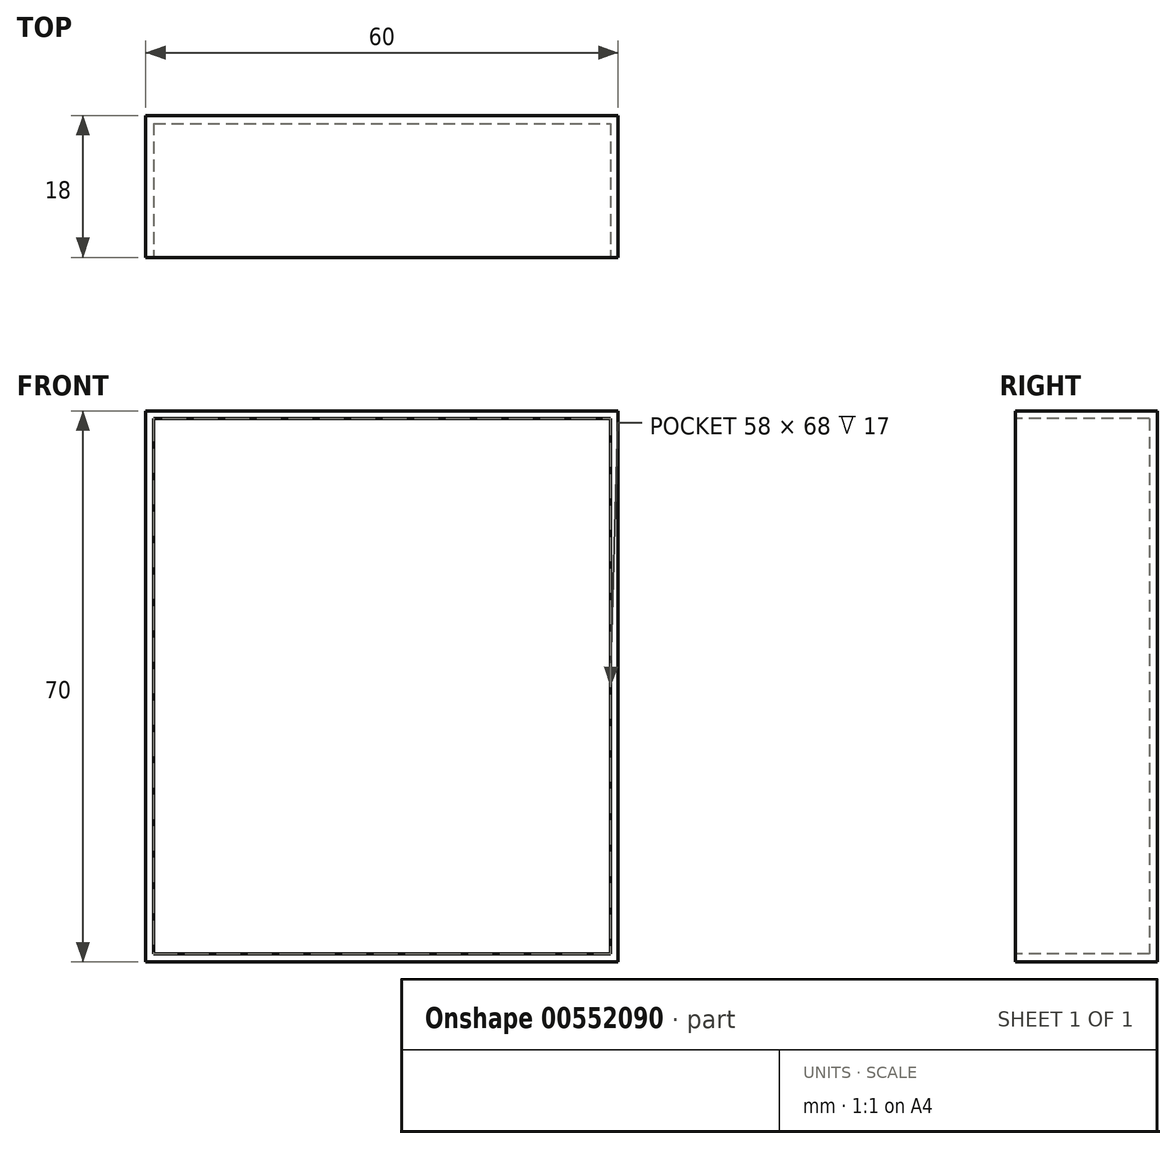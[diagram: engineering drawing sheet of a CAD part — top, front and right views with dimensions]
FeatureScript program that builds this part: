
annotation { "Feature Type Name" : "Feature", "Feature Type Description" : "" }
export const myFeature = defineFeature(function(context is Context, id is Id, definition is map)
    precondition{}
    {
        {
            var Q0;
            Q0=qCreatedBy(makeId("Front.planeOp"),FACE);
            var sketch = newSketch(context, id + "F0", { "sketchPlane" : qUnion([Q0])});
            skLineSegment(sketch, "E0.bottom", {"start": v(-30, 35) * mm, "end": v(30, 35) * mm});
            skLineSegment(sketch, "E0.top", {"start": v(-30, -35) * mm, "end": v(30, -35) * mm});
            skLineSegment(sketch, "E0.left", {"start": v(-30, 35) * mm, "end": v(-30, -35) * mm});
            skLineSegment(sketch, "E0.right", {"start": v(30, 35) * mm, "end": v(30, -35) * mm});
            skPoint(sketch, "E0.middle", {"position": v(0, 0) * mm});
            skSolve(sketch);
        }
        {
            var Q0;
            Q0 = qSketchRegion(id + "F0", true);
            extrude(context, id + "F1", {"entities" : qUnion([Q0]), "oppositeDirection" : true, "depth" : 18 * mm, "offsetDistance" : 25.4 * mm});
        }
        {
            var Q0;
            Q0=makeQuery(id+"F1.opExtrude","CAP_FACE",FACE,{"disambiguationData":[OSD([sQuery(id+"F0.wireOp",EDGE,"E0.bottom"),sQuery(id+"F0.wireOp",EDGE,"E0.top"),sQuery(id+"F0.wireOp",EDGE,"E0.left"),sQuery(id+"F0.wireOp",EDGE,"E0.right")])],"isStart":true});
            shell(context, id + "F2", {"entities" : qUnion([Q0]), "thickness" : 1 * mm});
        }
    });
